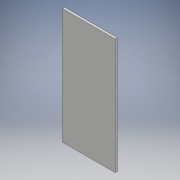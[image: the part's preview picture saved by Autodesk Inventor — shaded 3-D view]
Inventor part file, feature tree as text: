
AUTODESK INVENTOR PART (.ipt)
format: ipt  version: 2018 (Build 220112000, 112)  size: 92,672 bytes
history: native  units: mm
features: sketch x2, extrude x1
ambient origin geometry x8: Origin, YZ Plane, XZ Plane, XY Plane, X Axis, Y Axis, Z Axis, Center Point
bodies: 实体1 (feature_tree)
feature tree (3):
  extrude  "拉伸1"  Depth=55.0mm
  sketch  "草图2"  dims[d2=1.0mm d3=0.0mm]
  sketch  "草图1"  dims[d0=25.0mm d1=55.0mm]
